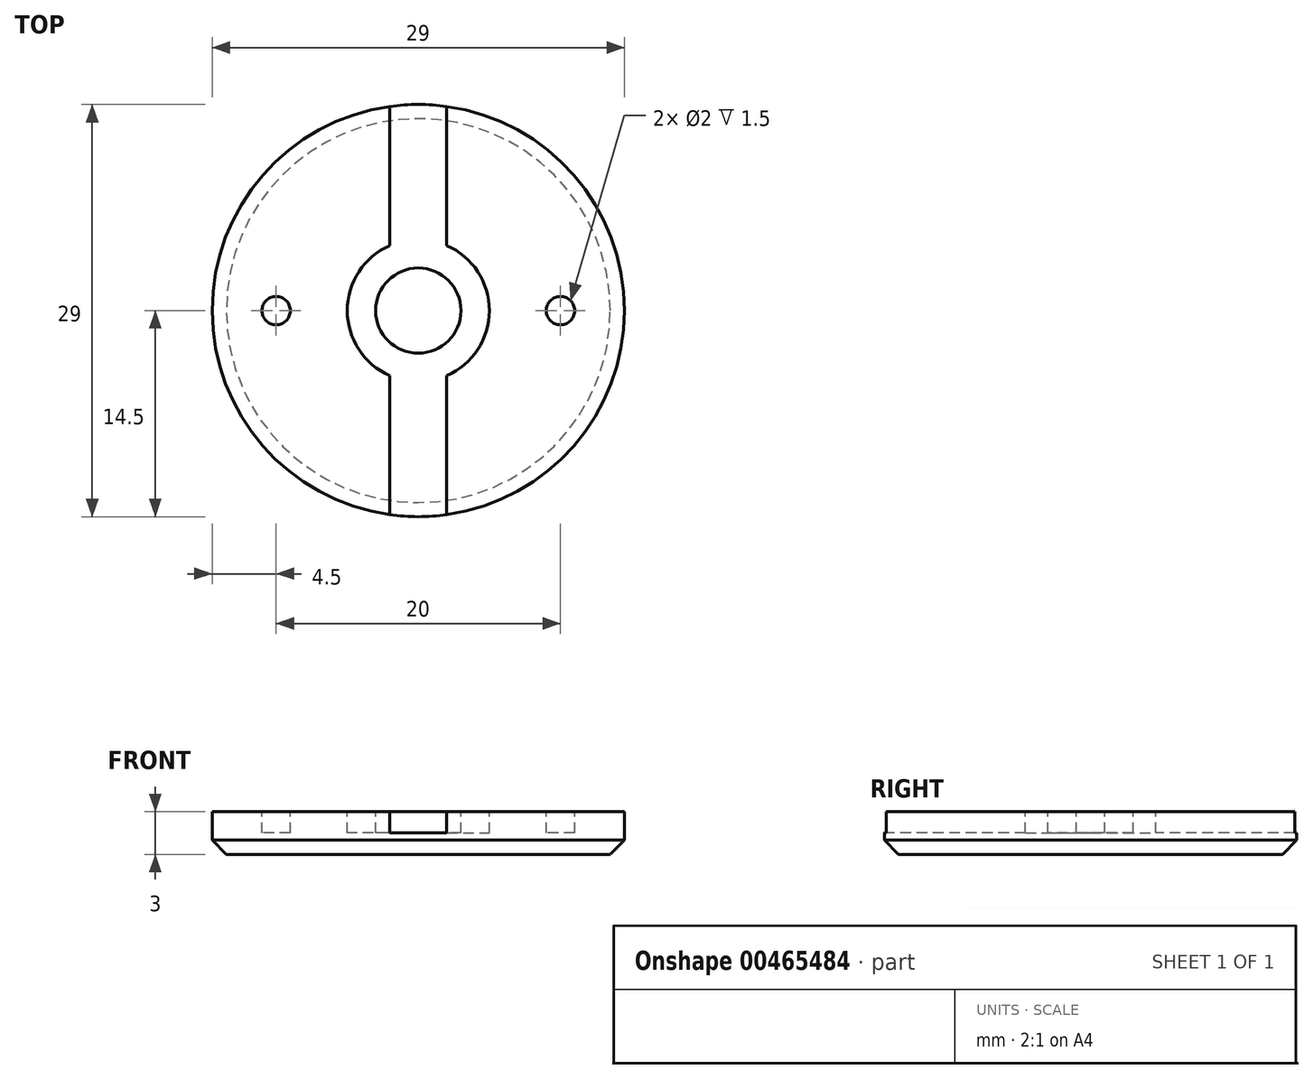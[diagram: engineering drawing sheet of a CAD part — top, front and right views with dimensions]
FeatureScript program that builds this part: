
annotation { "Feature Type Name" : "Feature", "Feature Type Description" : "" }
export const myFeature = defineFeature(function(context is Context, id is Id, definition is map)
    precondition{}
    {
        {
            var Q0;
            Q0=qCreatedBy(makeId("Top.planeOp"),FACE);
            var sketch = newSketch(context, id + "F0", { "sketchPlane" : qUnion([Q0])});
            skCircle(sketch, "E0", {"center": v(0, 0) * mm, "radius": 14.5 * mm});
            skSolve(sketch);
        }
        {
            var Q0;
            Q0 = qSketchRegion(id + "F0", true);
            extrude(context, id + "F1", {"entities" : qUnion([Q0]), "depth" : 3 * mm});
        }
        {
            var Q0;
            Q0=makeQuery(id+"F1.opExtrude","CAP_FACE",FACE,{"disambiguationData":[OSD([sQuery(id+"F0.wireOp",EDGE,"E0")])],"isStart":false});
            var sketch = newSketch(context, id + "F2", { "sketchPlane" : qUnion([Q0])});
            skLineSegment(sketch, "E1.bottom", {"start": v(-2, 15) * mm, "end": v(2, 15) * mm});
            skLineSegment(sketch, "E1.top", {"start": v(-2, -15) * mm, "end": v(2, -15) * mm});
            skLineSegment(sketch, "E1.left", {"start": v(-2, 15) * mm, "end": v(-2, -15) * mm});
            skLineSegment(sketch, "E1.right", {"start": v(2, 15) * mm, "end": v(2, -15) * mm});
            skSolve(sketch);
        }
        {
            var Q0;
            Q0 = qSketchRegion(id + "F2", true);
            extrude(context, id + "F3", {"entities" : qUnion([Q0]), "operationType" : NewBodyOperationType.REMOVE, "oppositeDirection" : true, "depth" : 1.5 * mm});
        }
        {
            var Q0;
            {var subQ0=sQuery(id+"F0.wireOp",EDGE,"E0");Q0=makeQuery(id+"F3.boolean.opBoolean","SPLIT",FACE,{"disambiguationData":[TD([makeQuery(id+"F3.opExtrude","SWEPT_FACE",FACE,{"disambiguationData":[OSD([sQuery(id+"F2.wireOp",EDGE,"E1.left")])]})])],"derivedFrom":makeQuery(id+"F1.opExtrude","CAP_FACE",FACE,{"disambiguationData":[OSD([subQ0])],"isStart":false})});}
            var sketch = newSketch(context, id + "F4", { "sketchPlane" : qUnion([Q0])});
            skCircle(sketch, "E2", {"center": v(0, 0) * mm, "radius": 5 * mm});
            skCircle(sketch, "E3", {"center": v(0, 0) * mm, "radius": 3 * mm});
            skSolve(sketch);
        }
        {
            var Q0;
            Q0 = qSketchRegion(id + "F4", true);
            extrude(context, id + "F5", {"entities" : qUnion([Q0]), "operationType" : NewBodyOperationType.REMOVE, "oppositeDirection" : true, "depth" : 1.5 * mm});
        }
        {
            var Q0;
            {var subQ0=sQuery(id+"F0.wireOp",EDGE,"E0");var subQ1=makeQuery(id+"F1.opExtrude","SWEPT_FACE",FACE,{"disambiguationData":[OSD([subQ0])]});var subQ2=makeQuery(id+"F3.opExtrude","SWEPT_FACE",FACE,{"disambiguationData":[OSD([sQuery(id+"F2.wireOp",EDGE,"E1.left")])]});Q0=makeQuery(id+"F5.boolean.opBoolean","SPLIT",FACE,{"disambiguationData":[TD([subQ1])],"derivedFrom":makeQuery(id+"F3.boolean.opBoolean","SPLIT",FACE,{"disambiguationData":[TD([subQ2])],"derivedFrom":makeQuery(id+"F1.opExtrude","CAP_FACE",FACE,{"disambiguationData":[OSD([subQ0])],"isStart":false})})});}
            var sketch = newSketch(context, id + "F6", { "sketchPlane" : qUnion([Q0])});
            skCircle(sketch, "E4", {"center": v(0, 0) * mm, "radius": 3 * mm});
            skSolve(sketch);
        }
        {
            var Q0;
            Q0 = qSketchRegion(id + "F6", true);
            extrude(context, id + "F7", {"entities" : qUnion([Q0]), "operationType" : NewBodyOperationType.ADD, "oppositeDirection" : true, "depth" : 1.5 * mm});
        }
        {
            var Q0;
            {var subQ0=sQuery(id+"F0.wireOp",EDGE,"E0");var subQ1=makeQuery(id+"F1.opExtrude","SWEPT_FACE",FACE,{"disambiguationData":[OSD([subQ0])]});var subQ2=makeQuery(id+"F3.opExtrude","SWEPT_FACE",FACE,{"disambiguationData":[OSD([sQuery(id+"F2.wireOp",EDGE,"E1.right")])]});Q0=makeQuery(id+"F5.boolean.opBoolean","SPLIT",FACE,{"disambiguationData":[TD([subQ1])],"derivedFrom":makeQuery(id+"F3.boolean.opBoolean","SPLIT",FACE,{"disambiguationData":[TD([subQ2])],"derivedFrom":makeQuery(id+"F1.opExtrude","CAP_FACE",FACE,{"disambiguationData":[OSD([subQ0])],"isStart":false})})});}
            var sketch = newSketch(context, id + "F8", { "sketchPlane" : qUnion([Q0])});
            skCircle(sketch, "E5", {"center": v(10, 0) * mm, "radius": 1 * mm});
            skCircle(sketch, "E6", {"center": v(-10, 0) * mm, "radius": 1 * mm});
            skSolve(sketch);
        }
        {
            var Q0;
            Q0 = qSketchRegion(id + "F8", true);
            extrude(context, id + "F9", {"entities" : qUnion([Q0]), "operationType" : NewBodyOperationType.REMOVE, "oppositeDirection" : true, "depth" : 1.5 * mm});
        }
        {
            var Q0;
            Q0=makeQuery(id+"F1.opExtrude","CAP_EDGE",EDGE,{"disambiguationData":[OSD([sQuery(id+"F0.wireOp",EDGE,"E0")])],"isStart":true});
            chamfer(context, id + "F10", {"entities" : qUnion([Q0]), "width" : 1 * mm, "tangentPropagation" : true});
        }
    });
